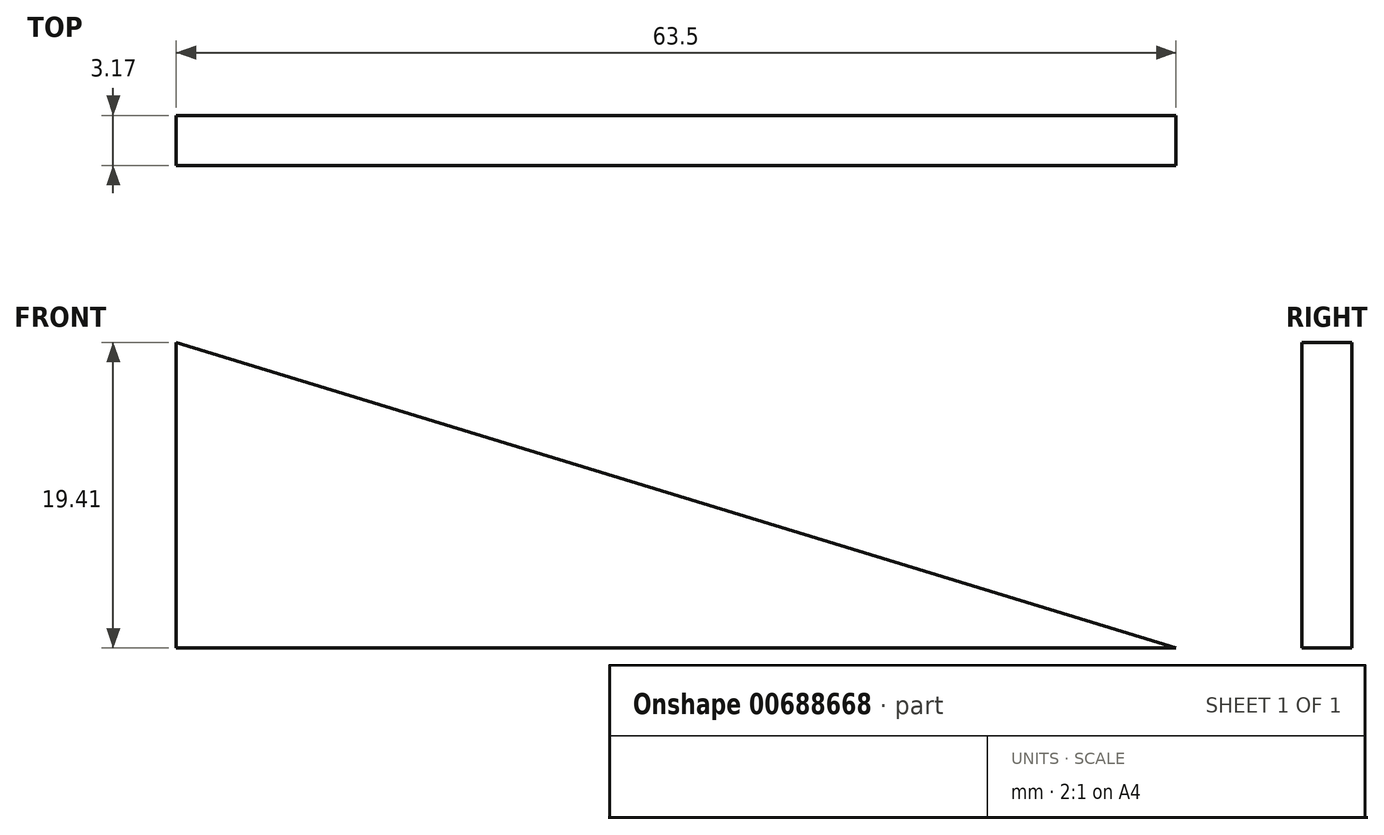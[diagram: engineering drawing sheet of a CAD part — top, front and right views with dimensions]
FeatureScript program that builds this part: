
annotation { "Feature Type Name" : "Feature", "Feature Type Description" : "" }
export const myFeature = defineFeature(function(context is Context, id is Id, definition is map)
    precondition{}
    {
        {
            var Q0;
            Q0=qCreatedBy(makeId("Front.planeOp"),FACE);
            var sketch = newSketch(context, id + "F0", { "sketchPlane" : qUnion([Q0])});
            skLineSegment(sketch, "E0", {"start": v(31.04, -34.48) * mm, "end": v(-32.46, -34.48) * mm});
            skLineSegment(sketch, "E1", {"start": v(31.04, -34.48) * mm, "end": v(-32.46, -15.07) * mm});
            skLineSegment(sketch, "E2", {"start": v(-32.46, -34.48) * mm, "end": v(-32.46, -15.07) * mm});
            skSolve(sketch);
        }
        {
            var Q0;
            Q0=makeQuery(id+"F0.imprint","IMPRINT",FACE,{"disambiguationData":[TD([[makeQuery(id+"F0.imprint","IMPRINT",EDGE,{"derivedFrom":sQuery(id+"F0.wireOp",EDGE,"E0")}),-1.0]])]});
            extrude(context, id + "F1", {"entities" : qUnion([Q0]), "depth" : 3.17 * mm, "offsetDistance" : 25.4 * mm});
        }
    });
